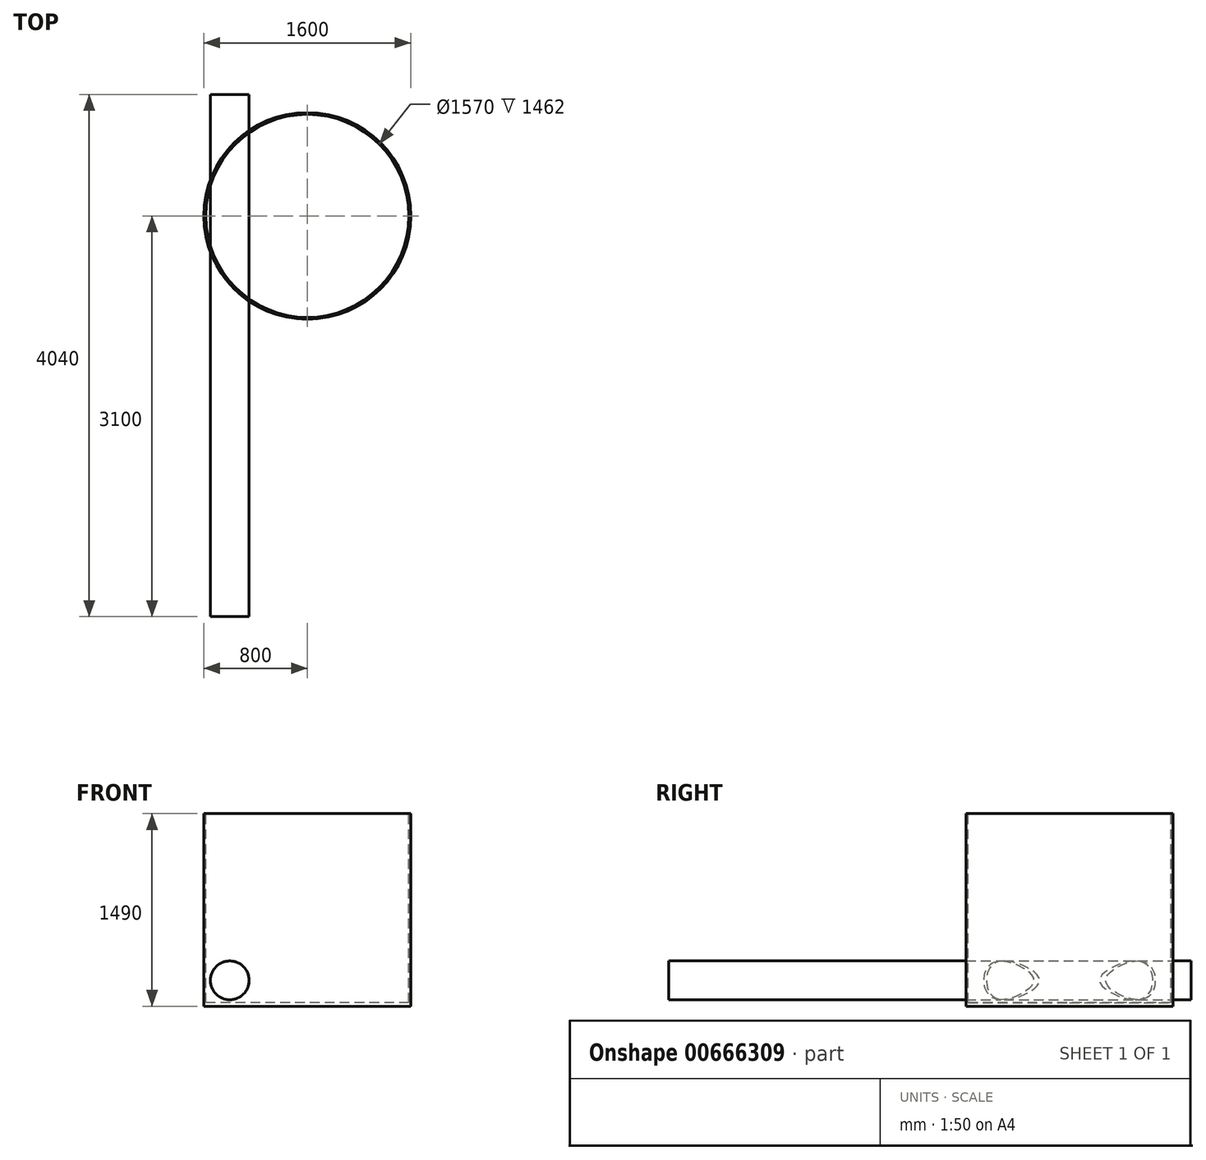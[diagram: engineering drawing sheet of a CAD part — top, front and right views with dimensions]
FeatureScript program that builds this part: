
annotation { "Feature Type Name" : "Feature", "Feature Type Description" : "" }
export const myFeature = defineFeature(function(context is Context, id is Id, definition is map)
    precondition{}
    {
        {
            var Q0;
            Q0=qCreatedBy(makeId("Top.planeOp"),FACE);
            var sketch = newSketch(context, id + "F0", { "sketchPlane" : qUnion([Q0])});
            skCircle(sketch, "E0", {"center": v(0, 0) * mm, "radius": 800 * mm});
            skSolve(sketch);
        }
        {
            var Q0;
            Q0=qSketchRegion(id+"F0",true);
            extrude(context, id + "F1", {"entities" : qUnion([Q0]), "depth" : (2640 - 1150) * mm});
        }
        {
            var Q0;
            Q0=makeQuery(id+"F1.opExtrude","CAP_FACE",FACE,{"disambiguationData":[OSD([sQuery(id+"F0.wireOp",EDGE,"E0")])],"isStart":false});
            var sketch = newSketch(context, id + "F2", { "sketchPlane" : qUnion([Q0])});
            skCircle(sketch, "E1", {"center": v(0, 0) * mm, "radius": 785 * mm});
            skSolve(sketch);
        }
        {
            var Q0;
            Q0=qSketchRegion(id+"F2",true);
            extrude(context, id + "F3", {"entities" : qUnion([Q0]), "operationType" : NewBodyOperationType.REMOVE, "oppositeDirection" : true, "depth" : 1462 * mm});
        }
        {
            var Q0;
            Q0=qCreatedBy(makeId("Front.planeOp"),FACE);
            var sketch = newSketch(context, id + "F4", { "sketchPlane" : qUnion([Q0])});
            skCircle(sketch, "E2", {"center": v(-600, 200) * mm, "radius": 150 * mm});
            skLineSegment(sketch, "E3", {"start": v(-800, 0) * mm, "end": v(-800, 627.99) * mm, "construction": true});
            skSolve(sketch);
        }
        {
            var Q0;
            Q0=qSketchRegion(id+"F4",true);
            extrude(context, id + "F5", {"entities" : qUnion([Q0]), "operationType" : NewBodyOperationType.ADD, "depth" : 3100 * mm, "hasSecondDirection" : true, "secondDirectionOppositeDirection" : true, "secondDirectionDepth" : 940 * mm});
        }
    });
